# Revit family: 業務用ロスナイ_外気処理ユニット
name_source: partatom
category: 機械設備
units: mm (PartAtom-declared; Revit-internal decimal feet)

## family parameters
OmniClass タイトル = Heat Exchangers for Ventilation Air
OmniClass 番号 = 23.75.10.34.21
パーツ タイプ = 標準
ロード時にボイドで切り取り = いいえ
丸型コネクタ寸法 = 直径を使用
作業面ベース = いいえ
共有 = いいえ
常に垂直 = はい
部屋計算ポイント = はい

## types (3) — shared parameters
Box_Depth = 120  [stored 0.393701 ft]
Box_Height = 290  [stored 0.951444 ft]
Box_Width = 217  [stored 0.711942 ft]
Duct_Depth_SA_RA = 79
EAダクト接続口方向_変更 = いいえ
EAダクト接続口方向_通常 = はい
IfcExportAs = IfcAirToAirHeatRecoveryType
IfcExportType = ROTARYWHEEL
OAダクト接続口方向_変更 = いいえ
OAダクト接続口方向_通常 = はい
OmniClassCode = 23-27 23 19 11
URL = https://www.mitsubishielectric.co.jp
Uniclass2015Code = Pr_60_60_36_88
Uniclass2015Title = Thermal wheels
Uniclass2015Version = Systems v1.9
ドレン管_Depth = 29
ドレン管径 = 32 mm
メンテナンススペース = はい
仕様書バージョン = Version1.0
付属品_フィルター = 不織布フィルター
付属品_フィルター_還気 = 不織布フィルター
企業コード = 108420
冷媒ガス管_W = 312
冷媒液管_H = 55
冷媒液管_W = 52
分類コード = 50052504100070
初期抵抗 = 0.0 Pa
加湿給水管径 = 23 mm
参照している仕様書等のバージョン = 公共建築物標準仕様書（機械設備工事編）平成31年度版
周波数 = 50 Hz
呼称 = 全熱交換ユニット
形式 = 天井埋込ダクト形
本体マテリアル = 亜鉛めっき鋼板
極数 = 1
法定耐用年数 = 15
消費電力_加湿器 = 0 W
点検口 = はい
点検口2_Depth = 450
点検口2_Width = 450
点検口離隔 = 150
相 = 1
積算_科目 = 1 空気調和設備
符号 = HEU
給水管_Depth = 29
給水管_W = 452
製品リリース年月 = 2019/10/1
製品出荷対象 = 国内
製造元 = MITSUBISHI ELECTRIC
設置方法 = 天井吊(隠ぺい)形
説明 = 業務用ロスナイ 外気処理ユニット(天井埋込形加熱加湿付直膨タイプ)
負荷分類 = 10_ファンコイル類
運転質量 = 0.00 kg
電圧 = 200 V
zero-valued in all types: EAサイズ_W, OAサイズ_W, RAサイズ_W, SAサイズ_W, 価格

## per-type parameters (varying)
- LGH-N50RDF3: Box_H=37  [stored 0.121391 ft]; Box_W=529; Clearance Left=600; Clearance Top=333  [stored 1.09252 ft]; Depth=1501; Duct_Change_Center=124  [stored 0.406824 ft]; Duct_Depth_OA_EA=79; Duct_Height=137  [stored 0.449475 ft]; Duct_Height_SA=204; Duct_Pitch_OA_EA=745; Duct_Pitch_SA_RA=447; Duct_Width_RA=373  [stored 1.22375 ft]; EAサイズ_D=192  [stored 0.629921 ft]; Height=333  [stored 1.09252 ft]; MAX静圧=140.0 Pa; MAX風量=500.0 m³/h; MID静圧=99.0 Pa; MID風量=420.0 m³/h; MIN静圧=30.0 Pa; MIN風量=230.0 m³/h; OAサイズ_D=192  [stored 0.629921 ft]; RAサイズ_D=192  [stored 0.629921 ft]; SAサイズ_D=192  [stored 0.629921 ft]; Width=1016; エンタルピ交換効率_冷房=64.50%; エンタルピ交換効率_暖房=68.50%; ドレン管_H=33  [stored 0.108268 ft]; ドレン管_W=442; 冷媒ガス管_Depth=110; 冷媒ガス管_H=170  [stored 0.557743 ft]; 冷媒ガス管径=13 mm; 冷媒液管_Depth=105; 冷媒液管径=6 mm; 吊りボルト_高さ=52; 吊りボルトピッチ1=1064; 吊りボルトピッチ2=1489; 外気量=500.0 m³/h; 天吊金具_幅=20  [stored 0.0656168 ft]; 天吊金具_径=7  [stored 0.0229659 ft]; 実風量=500.0 m³/h; 排気量=500.0 m³/h; 有効加湿量=3.2; 機外静圧=140.0 Pa; 機外静圧_排気=140.0 Pa; 消費電力=300 W; 温度交換効率=70.00%; 点検口1_Center=450; 点検口1_Depth=450; 点検口1_Width=450; 点検口高さ=-333  [stored -1.09252 ft]; 給水管_H=124  [stored 0.406824 ft]; 製品質量=74.00 kg; 設計風量=500.0 m³/h; 質量=88.80 kg; 電動機出力=85 W; 面風速=4.4 m/s; 風量=500.0 m³/h; 騒音レベル(dB(A))=35
- LGH-N80RDF3-50: Box_H=59; Box_W=569; Clearance Left=800; Clearance Top=408; Depth=1765; Duct_Change_Center=161; Duct_Depth_OA_EA=83; Duct_Height=204; Duct_Height_SA=243; Duct_Pitch_OA_EA=917; Duct_Pitch_SA_RA=745; Duct_Width_RA=460; EAサイズ_D=242; Height=408; MAX静圧=165.0 Pa; MAX風量=800.0 m³/h; MID静圧=99.0 Pa; MID風量=620.0 m³/h; MIN静圧=26.0 Pa; MIN風量=320.0 m³/h; OAサイズ_D=242; RAサイズ_D=242; SAサイズ_D=242; Width=1231; エンタルピ交換効率_冷房=67.00%; エンタルピ交換効率_暖房=72.00%; ドレン管_H=31; ドレン管_W=428; 冷媒ガス管_Depth=115; 冷媒ガス管_H=195; 冷媒ガス管径=13 mm; 冷媒液管_Depth=110; 冷媒液管径=6 mm; 吊りボルト_高さ=0  [stored 0 ft]; 吊りボルトピッチ1=1271; 吊りボルトピッチ2=1419; 外気量=800.0 m³/h; 天吊金具_幅=30; 天吊金具_径=8  [stored 0.0262467 ft]; 実風量=800.0 m³/h; 排気量=800.0 m³/h; 有効加湿量=4.8; 機外静圧=165.0 Pa; 機外静圧_排気=165.0 Pa; 消費電力=490 W; 温度交換効率=71.00%; 点検口1_Center=640; 点検口1_Depth=600; 点検口1_Width=600; 点検口高さ=-408; 給水管_H=148; 製品質量=112.00 kg; 設計風量=800.0 m³/h; 質量=134.40 kg; 電動機出力=149 W; 面風速=4.5 m/s; 風量=800.0 m³/h; 騒音レベル(dB(A))=35
- LGH-N100RDF3-50: Box_H=59; Box_W=569; Clearance Left=800; Clearance Top=408; Depth=1765; Duct_Change_Center=161; Duct_Depth_OA_EA=83; Duct_Height=204; Duct_Height_SA=243; Duct_Pitch_OA_EA=917; Duct_Pitch_SA_RA=745; Duct_Width_RA=460; EAサイズ_D=242; Height=408; MAX静圧=160.0 Pa; MAX風量=1000.0 m³/h; MID静圧=116.0 Pa; MID風量=850.0 m³/h; MIN静圧=30.0 Pa; MIN風量=430.0 m³/h; OAサイズ_D=242; RAサイズ_D=242; SAサイズ_D=242; Width=1231; エンタルピ交換効率_冷房=66.00%; エンタルピ交換効率_暖房=70.50%; ドレン管_H=31; ドレン管_W=428; 冷媒ガス管_Depth=115; 冷媒ガス管_H=195; 冷媒ガス管径=16 mm; 冷媒液管_Depth=110; 冷媒液管径=10 mm; 吊りボルト_高さ=0  [stored 0 ft]; 吊りボルトピッチ1=1271; 吊りボルトピッチ2=1419; 外気量=1000.0 m³/h; 天吊金具_幅=30; 天吊金具_径=8  [stored 0.0262467 ft]; 実風量=1000.0 m³/h; 排気量=1000.0 m³/h; 有効加湿量=6.4; 機外静圧=160.0 Pa; 機外静圧_排気=160.0 Pa; 消費電力=620 W; 温度交換効率=70.00%; 点検口1_Center=640; 点検口1_Depth=600; 点検口1_Width=600; 点検口高さ=-408; 給水管_H=148; 製品質量=114.00 kg; 設計風量=1000.0 m³/h; 質量=136.80 kg; 電動機出力=231 W; 面風速=5.7 m/s; 風量=1000.0 m³/h; 騒音レベル(dB(A))=38

note: column(s) folded — value = type name in every type: モデル

note: [stored X ft] marks values corroborated as IEEE doubles in the binary element streams (Revit-internal decimal feet)

## geometry (parser evidence)
native form markers: Blend x2
no freeform markers — native parametric forms only
